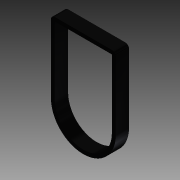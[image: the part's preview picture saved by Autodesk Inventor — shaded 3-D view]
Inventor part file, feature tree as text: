
AUTODESK INVENTOR PART (.ipt)
format: ipt  version: 2013 (Build 170138000, 138)  size: 88,576 bytes
history: native  units: in
note: dims shown in document units (in); Inventor stores cm internally (conversion verified against a paired STEP export)
features: reference x5, extrude x1, fillet x1, sketch x1
ambient origin geometry x8: Origin, YZ Plane, XZ Plane, XY Plane, X Axis, Y Axis, Z Axis, Center Point
bodies: Solid1 (feature_tree)
feature tree (8):
  extrude  "Extrusion1"  Depth=0.1378in TaperAngle=0.0deg
  fillet  "Fillet1"  Radius=0.0394in
  sketch  "Sketch1"  dims[d0=0.0394in d2=0.1378in d3=0.0in d4=0.0394in]
  reference  "Reference1"
  reference  "Reference2"
  reference  "Reference3"
  reference  "Reference4"
  reference  "Reference5"
